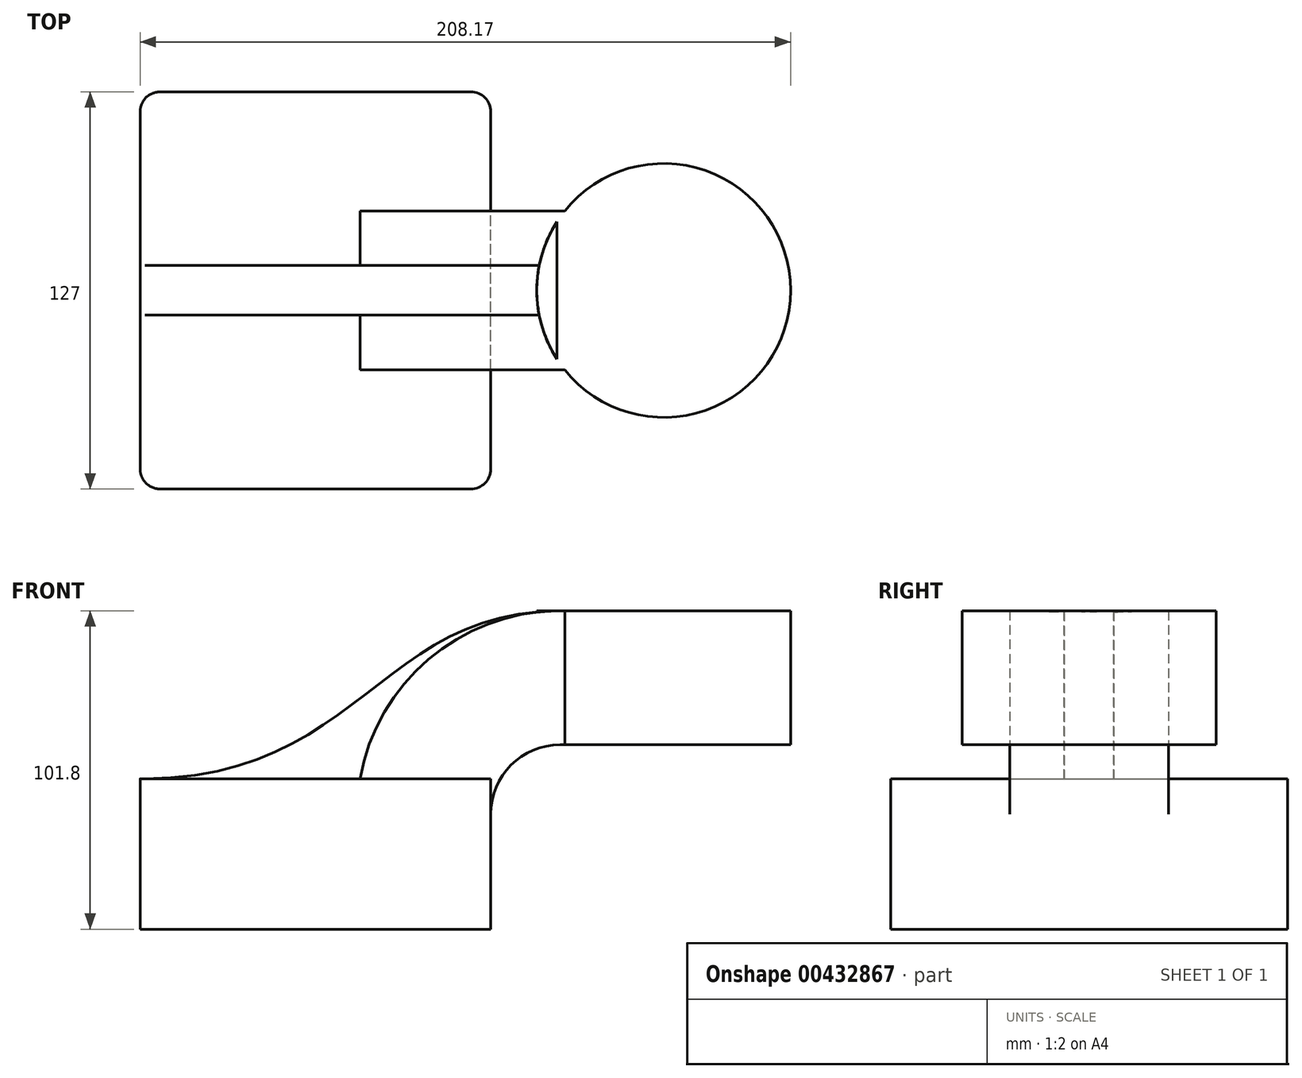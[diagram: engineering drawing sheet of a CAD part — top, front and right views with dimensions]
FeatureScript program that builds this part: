
annotation { "Feature Type Name" : "Feature", "Feature Type Description" : "" }
export const myFeature = defineFeature(function(context is Context, id is Id, definition is map)
    precondition{}
    {
        {
            var Q0;
            Q0=qCreatedBy(makeId("Front.planeOp"),FACE);
            var sketch = newSketch(context, id + "F0", { "sketchPlane" : qUnion([Q0])});
            skLineSegment(sketch, "E0.bottom", {"start": v(-56.1, 24.07) * mm, "end": v(56.1, 24.07) * mm});
            skLineSegment(sketch, "E0.top", {"start": v(-56.1, -24.07) * mm, "end": v(56.1, -24.07) * mm});
            skLineSegment(sketch, "E0.left", {"start": v(-56.1, 24.07) * mm, "end": v(-56.1, -24.07) * mm});
            skLineSegment(sketch, "E0.right", {"start": v(56.1, 24.07) * mm, "end": v(56.1, -24.07) * mm});
            skPoint(sketch, "E0.middle", {"position": v(0, 0) * mm});
            skLineSegment(sketch, "E1.bottom", {"start": v(111.45, 34.91) * mm, "end": v(152.07, 34.91) * mm});
            skLineSegment(sketch, "E1.top", {"start": v(111.45, 77.73) * mm, "end": v(152.07, 77.73) * mm});
            skLineSegment(sketch, "E1.left", {"start": v(111.45, 34.91) * mm, "end": v(111.45, 77.73) * mm});
            skLineSegment(sketch, "E1.right", {"start": v(152.07, 34.91) * mm, "end": v(152.07, 77.73) * mm});
            skPoint(sketch, "E1.middle", {"position": v(131.76, 56.32) * mm});
            skLineSegment(sketch, "E2", {"start": v(56.1, 12.72) * mm, "end": v(56.1, 24.07) * mm});
            skArc(sketch, "E3", {"start": v(56.1, 12.72) * mm, "mid": v(62.6, 28.41) * mm, "end": v(78.3, 34.91) * mm});
            skLineSegment(sketch, "E4", {"start": v(78.3, 34.91) * mm, "end": v(111.45, 34.91) * mm});
            skLineSegment(sketch, "E5.0", {"start": v(78.3, 77.73) * mm, "end": v(111.45, 77.73) * mm});
            skArc(sketch, "E5.1", {"start": v(14.28, 24.07) * mm, "mid": v(36.53, 62.54) * mm, "end": v(78.3, 77.73) * mm});
            skFitSpline(sketch, "E6", {"points": [v(-56.1, 24.07) * mm, v(78.3, 77.73) * mm], "startDerivative": vector(210.95, -1.18) * mm, "endDerivative": vector(175.5, 0.43) * mm});
            skSolve(sketch);
        }
        {
            var Q0;
            Q0=makeQuery(id+"F0.imprint","IMPRINT",FACE,{"disambiguationData":[TD([[makeQuery(id+"F0.imprint","IMPRINT",EDGE,{"derivedFrom":sQuery(id+"F0.wireOp",EDGE,"E1.left")}),1.0]])]});
            extrude(context, id + "F1", {"entities" : qUnion([Q0]), "endBound" : BoundingType.SYMMETRIC, "depth" : 50.8 * mm});
        }
        {
            var Q0;
            Q0=makeQuery(id+"F0.imprint","IMPRINT",FACE,{"disambiguationData":[TD([[makeQuery(id+"F0.imprint","IMPRINT",EDGE,{"derivedFrom":sQuery(id+"F0.wireOp",EDGE,"E0.top")}),1.0]])]});
            extrude(context, id + "F2", {"entities" : qUnion([Q0]), "operationType" : NewBodyOperationType.ADD, "endBound" : BoundingType.SYMMETRIC, "depth" : 127 * mm});
        }
        {
            var Q0;
            {var subQ0=sQuery(id+"F0.wireOp",EDGE,"E5.1");var subQ1=sQuery(id+"F0.wireOp",EDGE,"E0.bottom");var subQ2=makeQuery(id+"F0.imprint","INTERSECT",VERTEX,{"derivedFrom":[subQ1,subQ0]});Q0=makeQuery(id+"F0.imprint","IMPRINT",FACE,{"disambiguationData":[TD([[makeQuery(id+"F0.imprint","IMPRINT",EDGE,{"disambiguationData":[TD([[subQ2,1.0]])],"derivedFrom":subQ1}),1.0]])]});}
            extrude(context, id + "F3", {"entities" : qUnion([Q0]), "operationType" : NewBodyOperationType.ADD, "endBound" : BoundingType.SYMMETRIC, "depth" : 15.88 * mm});
        }
        {
            var Q0;
            Q0=makeQuery(id+"F0.imprint","IMPRINT",FACE,{"disambiguationData":[TD([[makeQuery(id+"F0.imprint","IMPRINT",EDGE,{"derivedFrom":sQuery(id+"F0.wireOp",EDGE,"E1.bottom")}),1.0]])]});
            var Q1;
            Q1=sQuery(id+"F0.wireOp",EDGE,"E1.left");
            revolve(context, id + "F4", {"operationType" : NewBodyOperationType.ADD, "entities" : qUnion([Q0]), "axis" : qUnion([Q1]), "revolveType" : RevolveType.FULL});
        }
        {
            var Q0;
            Q0=makeQuery(id+"F2.opExtrude","CAP_EDGE",EDGE,{"disambiguationData":[OSD([sQuery(id+"F0.wireOp",EDGE,"E0.left")])],"isStart":false});
            var Q1;
            Q1=makeQuery(id+"F2.opExtrude","CAP_EDGE",EDGE,{"disambiguationData":[OSD([sQuery(id+"F0.wireOp",EDGE,"E0.right"),sQuery(id+"F0.wireOp",EDGE,"E2")])],"isStart":false});
            var Q2;
            Q2=makeQuery(id+"F2.opExtrude","CAP_EDGE",EDGE,{"disambiguationData":[OSD([sQuery(id+"F0.wireOp",EDGE,"E0.left")])],"isStart":true});
            var Q3;
            Q3=makeQuery(id+"F2.opExtrude","CAP_EDGE",EDGE,{"disambiguationData":[OSD([sQuery(id+"F0.wireOp",EDGE,"E0.right"),sQuery(id+"F0.wireOp",EDGE,"E2")])],"isStart":true});
            fillet(context, id + "F5", {"entities" : qUnion([Q0, Q1, Q2, Q3]), "radius" : 6.35 * mm, "tangentPropagation" : true, "allowEdgeOverflow" : false});
        }
    });
